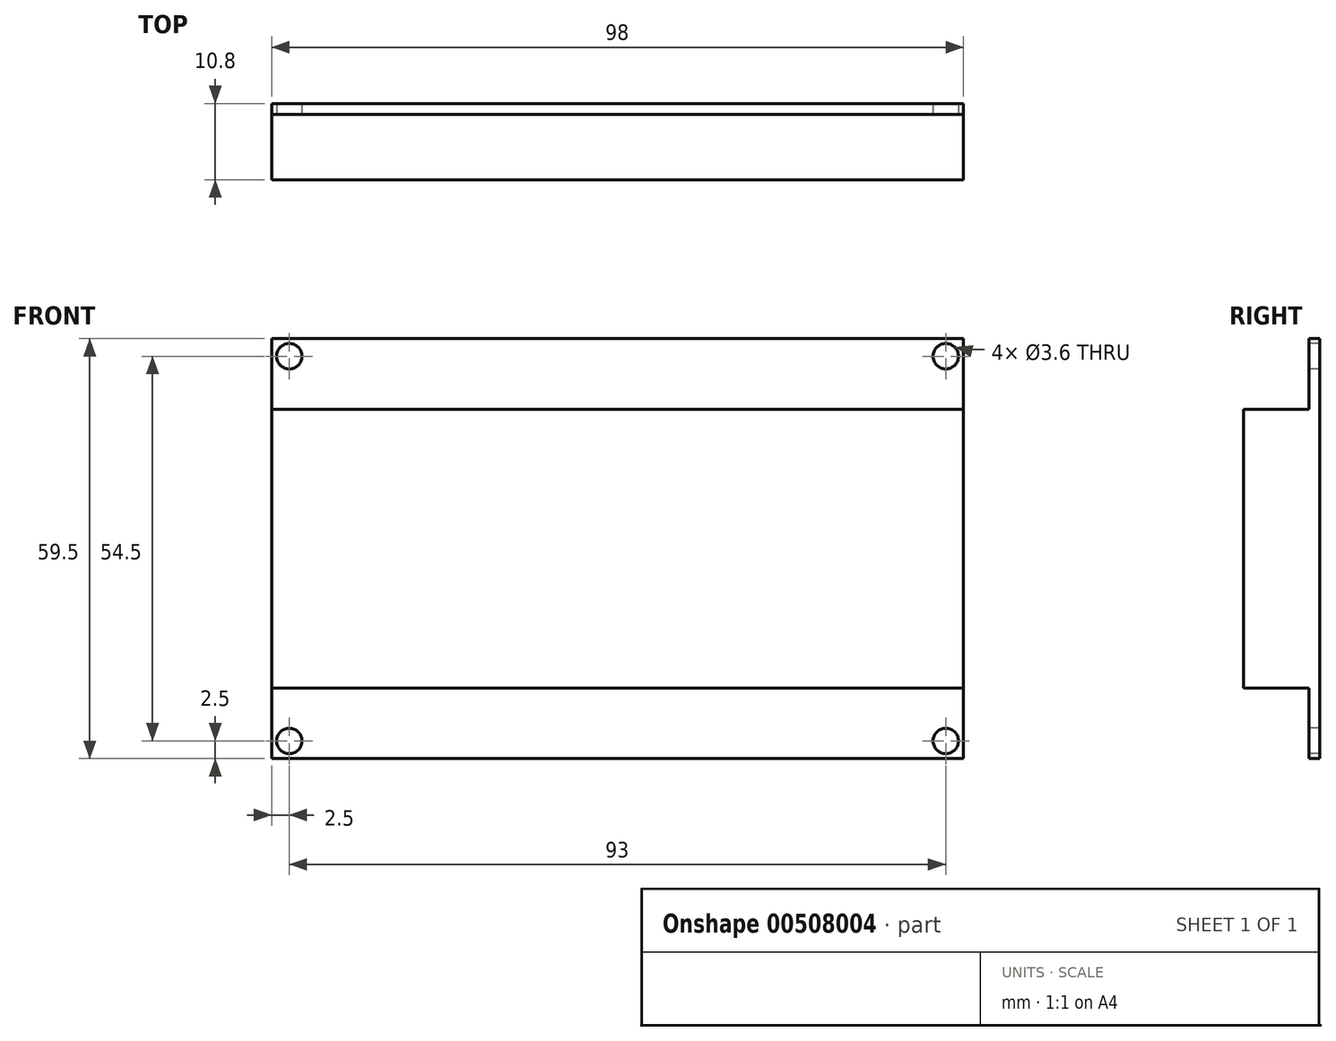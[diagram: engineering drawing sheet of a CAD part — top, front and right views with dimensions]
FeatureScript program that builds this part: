
annotation { "Feature Type Name" : "Feature", "Feature Type Description" : "" }
export const myFeature = defineFeature(function(context is Context, id is Id, definition is map)
    precondition{}
    {
        {
            var Q0;
            Q0=qCreatedBy(makeId("Front.planeOp"),FACE);
            var sketch = newSketch(context, id + "F0", { "sketchPlane" : qUnion([Q0])});
            skLineSegment(sketch, "E0.bottom", {"start": v(-49, 29.75) * mm, "end": v(49, 29.75) * mm});
            skLineSegment(sketch, "E0.top", {"start": v(-49, -29.75) * mm, "end": v(49, -29.75) * mm});
            skLineSegment(sketch, "E0.left", {"start": v(-49, 29.75) * mm, "end": v(-49, -29.75) * mm});
            skLineSegment(sketch, "E0.right", {"start": v(49, 29.75) * mm, "end": v(49, -29.75) * mm});
            skSolve(sketch);
        }
        {
            var Q0;
            Q0=makeQuery(id+"F0.imprint","IMPRINT",FACE,{"disambiguationData":[TD([[makeQuery(id+"F0.imprint","IMPRINT",EDGE,{"derivedFrom":sQuery(id+"F0.wireOp",EDGE,"E0.bottom")}),-1.0]])]});
            extrude(context, id + "F1", {"entities" : qUnion([Q0]), "depth" : 1.55 * mm});
        }
        {
            var Q0;
            Q0=makeQuery(id+"F1.opExtrude","CAP_FACE",FACE,{"disambiguationData":[OSD([sQuery(id+"F0.wireOp",EDGE,"E0.bottom"),sQuery(id+"F0.wireOp",EDGE,"E0.top"),sQuery(id+"F0.wireOp",EDGE,"E0.left"),sQuery(id+"F0.wireOp",EDGE,"E0.right")])],"isStart":false});
            var sketch = newSketch(context, id + "F2", { "sketchPlane" : qUnion([Q0])});
            skLineSegment(sketch, "E1.bottom", {"start": v(-49, 19.75) * mm, "end": v(49, 19.75) * mm});
            skLineSegment(sketch, "E1.top", {"start": v(-49, -19.75) * mm, "end": v(49, -19.75) * mm});
            skLineSegment(sketch, "E1.left", {"start": v(-49, 19.75) * mm, "end": v(-49, -19.75) * mm});
            skLineSegment(sketch, "E1.right", {"start": v(49, 19.75) * mm, "end": v(49, -19.75) * mm});
            skSolve(sketch);
        }
        {
            var Q0;
            Q0=makeQuery(id+"F2.imprint","IMPRINT",FACE,{"disambiguationData":[TD([[makeQuery(id+"F2.imprint","IMPRINT",EDGE,{"derivedFrom":sQuery(id+"F2.wireOp",EDGE,"E1.bottom")}),-1.0]])]});
            extrude(context, id + "F3", {"entities" : qUnion([Q0]), "operationType" : NewBodyOperationType.ADD, "depth" : 9.25 * mm});
        }
        {
            var Q0;
            {var subQ0=sQuery(id+"F0.wireOp",EDGE,"E0.left");var subQ1=sQuery(id+"F0.wireOp",EDGE,"E0.right");var subQ2=sQuery(id+"F0.wireOp",EDGE,"E0.bottom");Q0=makeQuery(id+"F3.boolean.opBoolean","SPLIT",FACE,{"disambiguationData":[TD([makeQuery(id+"F1.opExtrude","SWEPT_FACE",FACE,{"disambiguationData":[OSD([subQ2])]})])],"derivedFrom":makeQuery(id+"F1.opExtrude","CAP_FACE",FACE,{"disambiguationData":[OSD([subQ2,sQuery(id+"F0.wireOp",EDGE,"E0.top"),subQ0,subQ1])],"isStart":false})});}
            var sketch = newSketch(context, id + "F4", { "sketchPlane" : qUnion([Q0])});
            skCircle(sketch, "E2", {"center": v(-46.5, 27.25) * mm, "radius": 1.8 * mm});
            skCircle(sketch, "E3", {"center": v(46.5, 27.25) * mm, "radius": 1.8 * mm});
            skCircle(sketch, "E4", {"center": v(-46.5, -27.25) * mm, "radius": 1.8 * mm});
            skCircle(sketch, "E5", {"center": v(46.5, -27.25) * mm, "radius": 1.8 * mm});
            skSolve(sketch);
        }
        {
            var Q0;
            Q0=makeQuery(id+"F4.imprint","IMPRINT",FACE,{"disambiguationData":[TD([[makeQuery(id+"F4.imprint","IMPRINT",EDGE,{"derivedFrom":sQuery(id+"F4.wireOp",EDGE,"E2")}),1.0]])]});
            var Q1;
            Q1=makeQuery(id+"F4.imprint","IMPRINT",FACE,{"disambiguationData":[TD([[makeQuery(id+"F4.imprint","IMPRINT",EDGE,{"derivedFrom":sQuery(id+"F4.wireOp",EDGE,"E4")}),1.0]])]});
            var Q2;
            Q2=makeQuery(id+"F4.imprint","IMPRINT",FACE,{"disambiguationData":[TD([[makeQuery(id+"F4.imprint","IMPRINT",EDGE,{"derivedFrom":sQuery(id+"F4.wireOp",EDGE,"E5")}),1.0]])]});
            var Q3;
            Q3=makeQuery(id+"F4.imprint","IMPRINT",FACE,{"disambiguationData":[TD([[makeQuery(id+"F4.imprint","IMPRINT",EDGE,{"derivedFrom":sQuery(id+"F4.wireOp",EDGE,"E3")}),1.0]])]});
            extrude(context, id + "F5", {"entities" : qUnion([Q0, Q1, Q2, Q3]), "operationType" : NewBodyOperationType.REMOVE, "oppositeDirection" : true, "depth" : 25 * mm});
        }
    });
